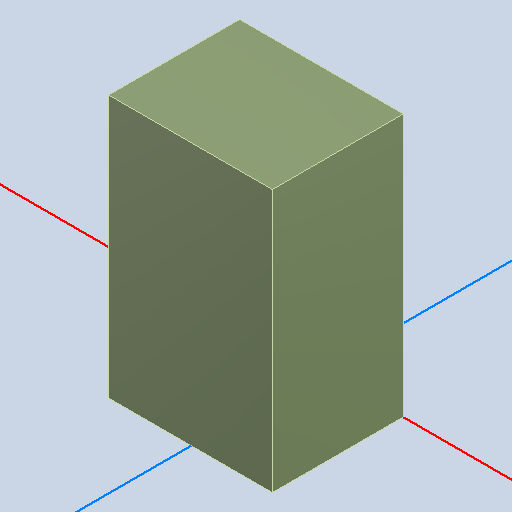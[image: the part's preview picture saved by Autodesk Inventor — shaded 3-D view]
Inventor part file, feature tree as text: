
AUTODESK INVENTOR PART (.ipt)
format: ipt  version: 2022 (Build 260153000, 153)  size: 95,232 bytes
history: native  units: mm
features: other x2, extrude x1
ambient origin geometry x8: Origin, YZ Plane, XZ Plane, XY Plane, X Axis, Y Axis, Z Axis, Center Point
bodies: Body1 (feature_tree)
feature tree (3):
  other  "Твердое тело1"
  extrude  "Выдавливание1"  Depth=1.0mm TaperAngle=0.0deg
  other  "CHIPLED_0805, CHIPLED_0805_19"
